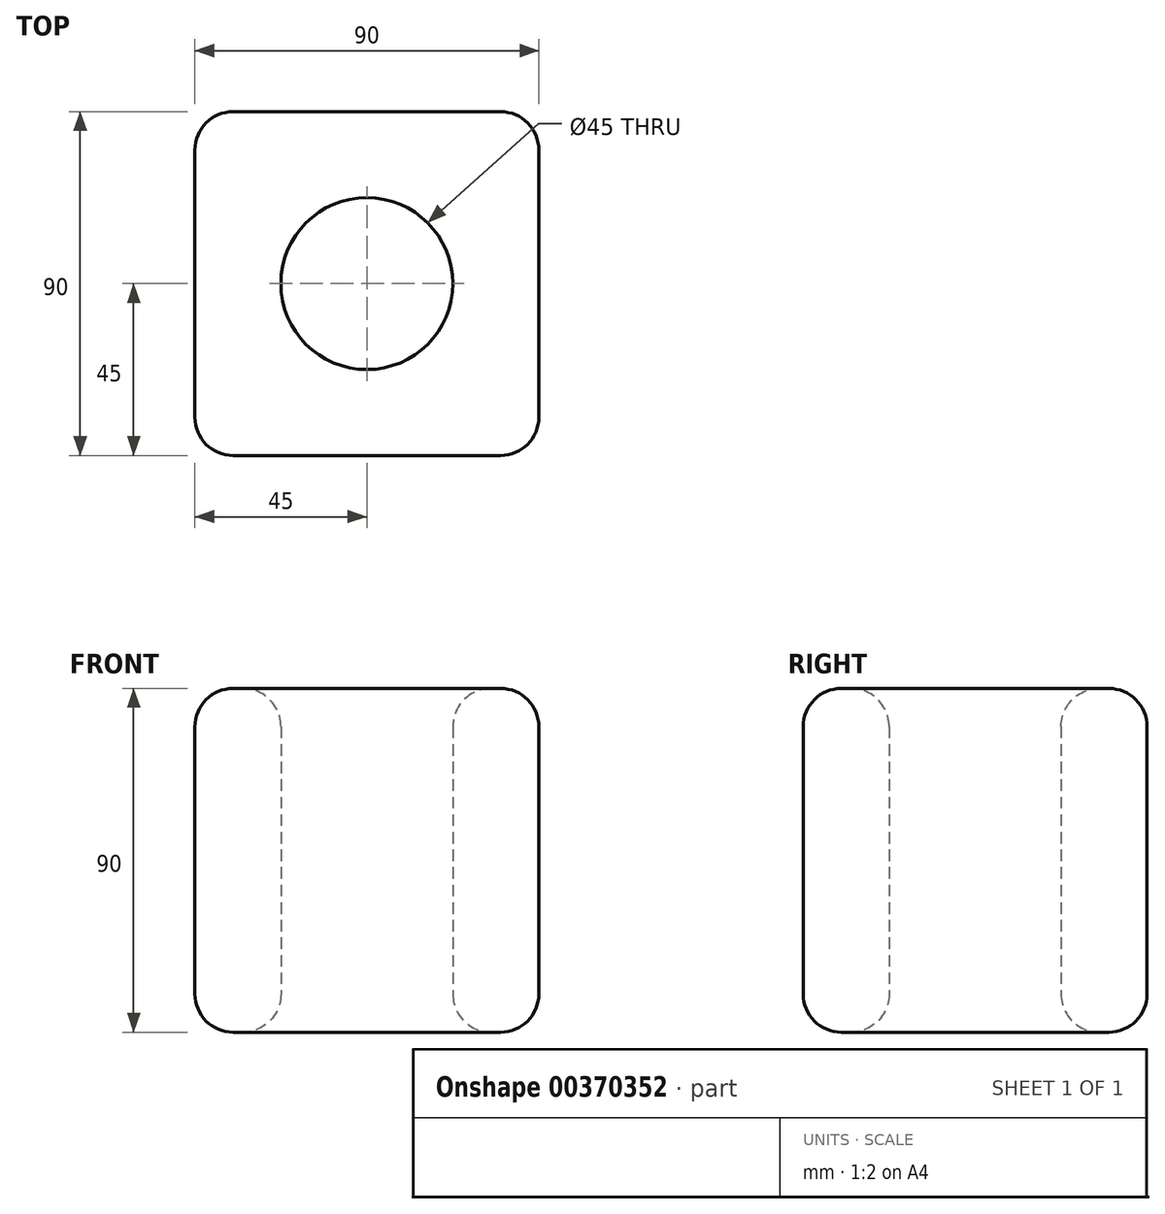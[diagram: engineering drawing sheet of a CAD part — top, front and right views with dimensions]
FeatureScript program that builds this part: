
annotation { "Feature Type Name" : "Feature", "Feature Type Description" : "" }
export const myFeature = defineFeature(function(context is Context, id is Id, definition is map)
    precondition{}
    {
        {
            var Q0;
            Q0=qCreatedBy(makeId("Top.planeOp"),FACE);
            var sketch = newSketch(context, id + "F0", { "sketchPlane" : qUnion([Q0])});
            skLineSegment(sketch, "E0.bottom", {"start": v(45, 45) * mm, "end": v(-45, 45) * mm});
            skLineSegment(sketch, "E0.top", {"start": v(45, -45) * mm, "end": v(-45, -45) * mm});
            skLineSegment(sketch, "E0.left", {"start": v(45, 45) * mm, "end": v(45, -45) * mm});
            skLineSegment(sketch, "E0.right", {"start": v(-45, 45) * mm, "end": v(-45, -45) * mm});
            skPoint(sketch, "E0.middle", {"position": v(0, 0) * mm});
            skCircle(sketch, "E1", {"center": v(0, 0) * mm, "radius": 22.5 * mm});
            skSolve(sketch);
        }
        {
            var Q0;
            Q0=makeQuery(id+"F0.imprint","IMPRINT",FACE,{"disambiguationData":[TD([[makeQuery(id+"F0.imprint","IMPRINT",EDGE,{"derivedFrom":sQuery(id+"F0.wireOp",EDGE,"E0.bottom")}),1.0]])]});
            extrude(context, id + "F1", {"entities" : qUnion([Q0]), "depth" : 90 * mm});
        }
        {
            var Q0;
            Q0=makeQuery(id+"F1.opExtrude","CAP_EDGE",EDGE,{"disambiguationData":[OSD([sQuery(id+"F0.wireOp",EDGE,"E1")])],"isStart":false});
            var Q1;
            Q1=makeQuery(id+"F1.opExtrude","CAP_EDGE",EDGE,{"disambiguationData":[OSD([sQuery(id+"F0.wireOp",EDGE,"E1")])],"isStart":true});
            var Q2;
            Q2=makeQuery(id+"F1.opExtrude","CAP_EDGE",EDGE,{"disambiguationData":[OSD([sQuery(id+"F0.wireOp",EDGE,"E0.top")])],"isStart":false});
            var Q3;
            Q3=makeQuery(id+"F1.opExtrude","CAP_EDGE",EDGE,{"disambiguationData":[OSD([sQuery(id+"F0.wireOp",EDGE,"E0.left")])],"isStart":false});
            var Q4;
            Q4=makeQuery(id+"F1.opExtrude","CAP_EDGE",EDGE,{"disambiguationData":[OSD([sQuery(id+"F0.wireOp",EDGE,"E0.bottom")])],"isStart":false});
            var Q5;
            Q5=makeQuery(id+"F1.opExtrude","CAP_EDGE",EDGE,{"disambiguationData":[OSD([sQuery(id+"F0.wireOp",EDGE,"E0.right")])],"isStart":false});
            var Q6;
            Q6=makeQuery(id+"F1.opExtrude","CAP_EDGE",EDGE,{"disambiguationData":[OSD([sQuery(id+"F0.wireOp",EDGE,"E0.right")])],"isStart":true});
            var Q7;
            Q7=makeQuery(id+"F1.opExtrude","CAP_EDGE",EDGE,{"disambiguationData":[OSD([sQuery(id+"F0.wireOp",EDGE,"E0.bottom")])],"isStart":true});
            var Q8;
            Q8=makeQuery(id+"F1.opExtrude","CAP_EDGE",EDGE,{"disambiguationData":[OSD([sQuery(id+"F0.wireOp",EDGE,"E0.left")])],"isStart":true});
            var Q9;
            Q9=makeQuery(id+"F1.opExtrude","CAP_EDGE",EDGE,{"disambiguationData":[OSD([sQuery(id+"F0.wireOp",EDGE,"E0.top")])],"isStart":true});
            var Q10;
            Q10=makeQuery(id+"F1.opExtrude","SWEPT_EDGE",EDGE,{"disambiguationData":[OSD([sQuery(id+"F0.wireOp",EDGE,"E0.top"),sQuery(id+"F0.wireOp",EDGE,"E0.left")])]});
            var Q11;
            Q11=makeQuery(id+"F1.opExtrude","SWEPT_EDGE",EDGE,{"disambiguationData":[OSD([sQuery(id+"F0.wireOp",EDGE,"E0.top"),sQuery(id+"F0.wireOp",EDGE,"E0.right")])]});
            var Q12;
            Q12=makeQuery(id+"F1.opExtrude","SWEPT_EDGE",EDGE,{"disambiguationData":[OSD([sQuery(id+"F0.wireOp",EDGE,"E0.bottom"),sQuery(id+"F0.wireOp",EDGE,"E0.right")])]});
            var Q13;
            Q13=makeQuery(id+"F1.opExtrude","SWEPT_EDGE",EDGE,{"disambiguationData":[OSD([sQuery(id+"F0.wireOp",EDGE,"E0.bottom"),sQuery(id+"F0.wireOp",EDGE,"E0.left")])]});
            fillet(context, id + "F2", {"entities" : qUnion([Q0, Q1, Q2, Q3, Q4, Q5, Q6, Q7, Q8, Q9, Q10, Q11, Q12, Q13]), "radius" : 10 * mm, "tangentPropagation" : true, "allowEdgeOverflow" : false});
        }
    });
